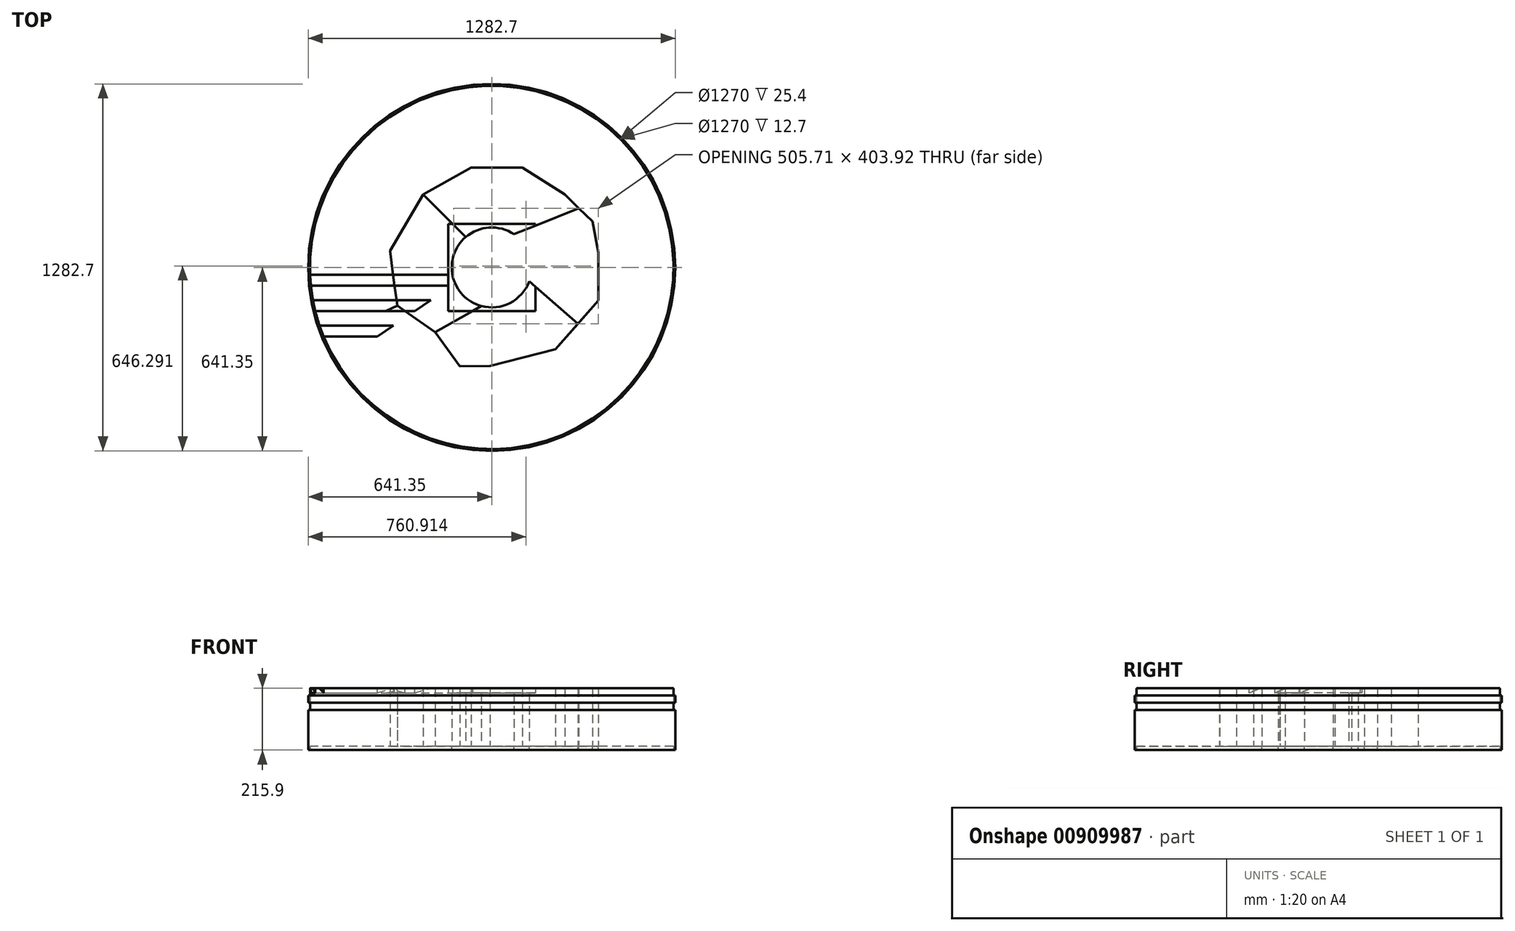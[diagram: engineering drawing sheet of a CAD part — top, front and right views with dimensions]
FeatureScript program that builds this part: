
annotation { "Feature Type Name" : "Feature", "Feature Type Description" : "" }
export const myFeature = defineFeature(function(context is Context, id is Id, definition is map)
    precondition{}
    {
        {
            var Q0;
            Q0=qCreatedBy(makeId("Top.planeOp"),FACE);
            var sketch = newSketch(context, id + "F0", { "sketchPlane" : qUnion([Q0])});
            skCircle(sketch, "E0", {"center": v(0, 0) * mm, "radius": 139.7 * mm});
            skCircle(sketch, "E1", {"center": v(0, 0) * mm, "radius": 635 * mm});
            skLineSegment(sketch, "E2", {"start": v(-36.54, -134.84) * mm, "end": v(-197.5, -226.73) * mm});
            skLineSegment(sketch, "E3", {"start": v(-197.5, -226.73) * mm, "end": v(-330.22, -133.5) * mm});
            skLineSegment(sketch, "E4", {"start": v(-330.22, -133.5) * mm, "end": v(-355.5, 57.67) * mm});
            skLineSegment(sketch, "E5", {"start": v(-355.5, 57.67) * mm, "end": v(-238.95, 255.32) * mm});
            skLineSegment(sketch, "E6", {"start": v(-238.95, 255.32) * mm, "end": v(-91, 106) * mm});
            skLineSegment(sketch, "E7", {"start": v(-238.95, 255.32) * mm, "end": v(-71.47, 348.54) * mm});
            skLineSegment(sketch, "E8", {"start": v(-71.47, 348.54) * mm, "end": v(107.07, 348.54) * mm});
            skLineSegment(sketch, "E9", {"start": v(107.07, 348.54) * mm, "end": v(255.58, 255.32) * mm});
            skLineSegment(sketch, "E10", {"start": v(255.58, 255.32) * mm, "end": v(303.56, 206.9) * mm});
            skLineSegment(sketch, "E11", {"start": v(303.56, 206.9) * mm, "end": v(77.5, 116.24) * mm});
            skLineSegment(sketch, "E12", {"start": v(77.5, 116.24) * mm, "end": v(303.56, 206.9) * mm});
            skLineSegment(sketch, "E13", {"start": v(303.56, 206.9) * mm, "end": v(351.96, 160.52) * mm});
            skLineSegment(sketch, "E14", {"start": v(351.96, 160.52) * mm, "end": v(372.42, 52.06) * mm});
            skLineSegment(sketch, "E15", {"start": v(372.42, 52.06) * mm, "end": v(372.42, -115.42) * mm});
            skLineSegment(sketch, "E16", {"start": v(372.42, -115.42) * mm, "end": v(301.18, -197.02) * mm});
            skLineSegment(sketch, "E17", {"start": v(301.18, -197.02) * mm, "end": v(223.18, -286.36) * mm});
            skLineSegment(sketch, "E18", {"start": v(223.18, -286.36) * mm, "end": v(-5.86, -344.53) * mm});
            skLineSegment(sketch, "E19", {"start": v(-5.86, -344.53) * mm, "end": v(-110.6, -345.22) * mm});
            skLineSegment(sketch, "E20", {"start": v(-110.6, -345.22) * mm, "end": v(-197.5, -226.73) * mm});
            skLineSegment(sketch, "E21", {"start": v(301.18, -197.02) * mm, "end": v(131.02, -48.47) * mm});
            skLineSegment(sketch, "E22", {"start": v(-330.22, -133.5) * mm, "end": v(-582.73, -252.28) * mm});
            skLineSegment(sketch, "E23", {"start": v(-355.5, 57.67) * mm, "end": v(-618.8, 142.52) * mm});
            skLineSegment(sketch, "E24", {"start": v(-238.95, 255.32) * mm, "end": v(-456.44, 441.46) * mm});
            skLineSegment(sketch, "E25", {"start": v(-71.47, 348.54) * mm, "end": v(-141.76, 618.97) * mm});
            skLineSegment(sketch, "E26", {"start": v(107.07, 348.54) * mm, "end": v(221.56, 595.1) * mm});
            skLineSegment(sketch, "E27", {"start": v(255.58, 255.32) * mm, "end": v(450.04, 447.98) * mm});
            skLineSegment(sketch, "E28", {"start": v(351.96, 160.52) * mm, "end": v(600.2, 207.35) * mm});
            skLineSegment(sketch, "E29", {"start": v(372.42, 52.06) * mm, "end": v(633.2, -47.9) * mm});
            skLineSegment(sketch, "E30", {"start": v(372.42, -115.42) * mm, "end": v(570.5, -278.85) * mm});
            skLineSegment(sketch, "E31", {"start": v(223.18, -286.36) * mm, "end": v(344.95, -533.14) * mm});
            skLineSegment(sketch, "E32", {"start": v(-5.86, -344.53) * mm, "end": v(67, -631.45) * mm});
            skLineSegment(sketch, "E33", {"start": v(-110.6, -345.22) * mm, "end": v(-330.26, -542.36) * mm});
            skCircle(sketch, "E34", {"center": v(0, 0) * mm, "radius": 641.35 * mm});
            skSolve(sketch);
        }
        {
            var Q0;
            Q0=makeQuery(id+"F0.imprint","IMPRINT",FACE,{"disambiguationData":[TD([[makeQuery(id+"F0.imprint","IMPRINT",EDGE,{"derivedFrom":sQuery(id+"F0.wireOp",EDGE,"E0")}),-1.0]])]});
            var Q1;
            {var subQ0=sQuery(id+"F0.wireOp",EDGE,"E12");Q1=makeQuery(id+"F0.imprint","IMPRINT",FACE,{"disambiguationData":[TD([[makeQuery(id+"F0.imprint","IMPRINT",EDGE,{"derivedFrom":subQ0}),-1.0]])]});}
            var Q2;
            Q2=makeQuery(id+"F0.imprint","IMPRINT",FACE,{"disambiguationData":[TD([[makeQuery(id+"F0.imprint","IMPRINT",EDGE,{"derivedFrom":sQuery(id+"F0.wireOp",EDGE,"E9")}),1.0]])]});
            var Q3;
            Q3=makeQuery(id+"F0.imprint","IMPRINT",FACE,{"disambiguationData":[TD([[makeQuery(id+"F0.imprint","IMPRINT",EDGE,{"derivedFrom":sQuery(id+"F0.wireOp",EDGE,"E7")}),1.0]])]});
            var Q4;
            Q4=makeQuery(id+"F0.imprint","IMPRINT",FACE,{"disambiguationData":[TD([[makeQuery(id+"F0.imprint","IMPRINT",EDGE,{"derivedFrom":sQuery(id+"F0.wireOp",EDGE,"E19")}),1.0]])]});
            extrude(context, id + "F1", {"entities" : qUnion([Q0, Q1, Q2, Q3, Q4]), "depth" : 203.2 * mm, "offsetDistance" : 25 * mm});
        }
        {
            var Q0;
            {var subQ0=sQuery(id+"F0.wireOp",EDGE,"E2");Q0=makeQuery(id+"F0.imprint","IMPRINT",FACE,{"disambiguationData":[TD([[makeQuery(id+"F0.imprint","IMPRINT",EDGE,{"derivedFrom":subQ0}),1.0]])]});}
            var Q1;
            {var subQ0=sQuery(id+"F0.wireOp",EDGE,"E6");Q1=makeQuery(id+"F0.imprint","IMPRINT",FACE,{"disambiguationData":[TD([[makeQuery(id+"F0.imprint","IMPRINT",EDGE,{"derivedFrom":subQ0}),1.0]])]});}
            var Q2;
            Q2=makeQuery(id+"F0.imprint","IMPRINT",FACE,{"disambiguationData":[TD([[makeQuery(id+"F0.imprint","IMPRINT",EDGE,{"derivedFrom":sQuery(id+"F0.wireOp",EDGE,"E15")}),1.0]])]});
            var Q3;
            Q3=makeQuery(id+"F0.imprint","IMPRINT",FACE,{"disambiguationData":[TD([[makeQuery(id+"F0.imprint","IMPRINT",EDGE,{"derivedFrom":sQuery(id+"F0.wireOp",EDGE,"E4")}),1.0]])]});
            extrude(context, id + "F2", {"entities" : qUnion([Q0, Q1, Q2, Q3]), "depth" : 203.2 * mm, "offsetDistance" : 25 * mm});
        }
        {
            var Q0;
            Q0=makeQuery(id+"F0.imprint","IMPRINT",FACE,{"disambiguationData":[TD([[makeQuery(id+"F0.imprint","IMPRINT",EDGE,{"derivedFrom":sQuery(id+"F0.wireOp",EDGE,"E18")}),1.0]])]});
            var Q1;
            Q1=makeQuery(id+"F0.imprint","IMPRINT",FACE,{"disambiguationData":[TD([[makeQuery(id+"F0.imprint","IMPRINT",EDGE,{"derivedFrom":sQuery(id+"F0.wireOp",EDGE,"E3")}),1.0]])]});
            var Q2;
            Q2=makeQuery(id+"F0.imprint","IMPRINT",FACE,{"disambiguationData":[TD([[makeQuery(id+"F0.imprint","IMPRINT",EDGE,{"derivedFrom":sQuery(id+"F0.wireOp",EDGE,"E5")}),1.0]])]});
            var Q3;
            Q3=makeQuery(id+"F0.imprint","IMPRINT",FACE,{"disambiguationData":[TD([[makeQuery(id+"F0.imprint","IMPRINT",EDGE,{"derivedFrom":sQuery(id+"F0.wireOp",EDGE,"E8")}),1.0]])]});
            var Q4;
            Q4=makeQuery(id+"F0.imprint","IMPRINT",FACE,{"disambiguationData":[TD([[makeQuery(id+"F0.imprint","IMPRINT",EDGE,{"derivedFrom":sQuery(id+"F0.wireOp",EDGE,"E10")}),1.0]])]});
            extrude(context, id + "F3", {"entities" : qUnion([Q0, Q1, Q2, Q3, Q4]), "depth" : 203.2 * mm, "offsetDistance" : 25 * mm});
        }
        {
            var Q0;
            Q0=makeQuery(id+"F0.imprint","IMPRINT",FACE,{"disambiguationData":[TD([[makeQuery(id+"F0.imprint","IMPRINT",EDGE,{"derivedFrom":sQuery(id+"F0.wireOp",EDGE,"E16")}),1.0]])]});
            var Q1;
            Q1=makeQuery(id+"F0.imprint","IMPRINT",FACE,{"disambiguationData":[TD([[makeQuery(id+"F0.imprint","IMPRINT",EDGE,{"derivedFrom":sQuery(id+"F0.wireOp",EDGE,"E14")}),1.0]])]});
            extrude(context, id + "F4", {"entities" : qUnion([Q0, Q1]), "depth" : 203.2 * mm, "offsetDistance" : 25 * mm});
        }
        {
            var Q0;
            Q0=makeQuery(id+"F1.opExtrude","CAP_FACE",FACE,{"disambiguationData":[OSD([sQuery(id+"F0.wireOp",EDGE,"E0"),sQuery(id+"F0.wireOp",EDGE,"E1")])],"isStart":false});
            var sketch = newSketch(context, id + "F5", { "sketchPlane" : qUnion([Q0])});
            skLineSegment(sketch, "E35.bottom", {"start": v(-634.5, -25.4) * mm, "end": v(-138.54, -25.4) * mm});
            skLineSegment(sketch, "E35.top", {"start": v(-634.5, -63.5) * mm, "end": v(-138.54, -63.5) * mm});
            skLineSegment(sketch, "E35.left", {"start": v(-634.5, -25.4) * mm, "end": v(-634.5, -63.5) * mm});
            skLineSegment(sketch, "E35.right", {"start": v(-138.54, -25.4) * mm, "end": v(-138.54, -63.5) * mm});
            skLineSegment(sketch, "E36.bottom", {"start": v(-624.63, -114.3) * mm, "end": v(-213.24, -114.3) * mm});
            skLineSegment(sketch, "E36.top", {"start": v(-624.63, -152.4) * mm, "end": v(-269.26, -152.4) * mm});
            skLineSegment(sketch, "E36.left", {"start": v(-624.63, -114.3) * mm, "end": v(-624.63, -152.4) * mm});
            skLineSegment(sketch, "E37.bottom", {"start": v(-601.61, -203.2) * mm, "end": v(-343.96, -203.2) * mm});
            skLineSegment(sketch, "E37.top", {"start": v(-601.61, -241.3) * mm, "end": v(-399.98, -241.3) * mm});
            skLineSegment(sketch, "E37.left", {"start": v(-601.61, -203.2) * mm, "end": v(-601.61, -241.3) * mm});
            skLineSegment(sketch, "E38", {"start": v(-444.25, -25.4) * mm, "end": v(-444.25, -114.3) * mm, "construction": true});
            skLineSegment(sketch, "E39", {"start": v(-444.25, -114.3) * mm, "end": v(-444.25, -203.2) * mm, "construction": true});
            skLineSegment(sketch, "E40", {"start": v(-213.24, -114.3) * mm, "end": v(-269.26, -152.4) * mm});
            skLineSegment(sketch, "E41", {"start": v(-343.96, -203.2) * mm, "end": v(-399.98, -241.3) * mm});
            skCircle(sketch, "E42", {"center": v(0, 0) * mm, "radius": 152.4 * mm});
            skLineSegment(sketch, "E43.bottom", {"start": v(-152.4, 152.4) * mm, "end": v(152.4, 152.4) * mm});
            skLineSegment(sketch, "E43.top", {"start": v(-152.4, -152.4) * mm, "end": v(152.4, -152.4) * mm});
            skLineSegment(sketch, "E43.left", {"start": v(-152.4, 152.4) * mm, "end": v(-152.4, -152.4) * mm});
            skLineSegment(sketch, "E43.right", {"start": v(152.4, 152.4) * mm, "end": v(152.4, -152.4) * mm});
            skLineSegment(sketch, "E44", {"start": v(0, 152.4) * mm, "end": v(0, -152.4) * mm, "construction": true});
            skLineSegment(sketch, "E45", {"start": v(152.4, 0) * mm, "end": v(-152.4, 0) * mm, "construction": true});
            skSolve(sketch);
        }
        {
            var Q0;
            {var subQ0=sQuery(id+"F5.wireOp",EDGE,"E36.bottom");Q0=makeQuery(id+"F5.imprint","IMPRINT",FACE,{"disambiguationData":[TD([[makeQuery(id+"F5.imprint","IMPRINT",EDGE,{"derivedFrom":subQ0}),-1.0]])]});}
            var Q1;
            {var subQ0=sQuery(id+"F5.wireOp",EDGE,"E37.bottom");Q1=makeQuery(id+"F5.imprint","IMPRINT",FACE,{"disambiguationData":[TD([[makeQuery(id+"F5.imprint","IMPRINT",EDGE,{"derivedFrom":subQ0}),-1.0]])]});}
            var Q2;
            {var subQ0=sQuery(id+"F5.wireOp",EDGE,"E35.left");Q2=makeQuery(id+"F5.imprint","IMPRINT",FACE,{"disambiguationData":[TD([[makeQuery(id+"F5.imprint","IMPRINT",EDGE,{"derivedFrom":subQ0}),1.0]])]});}
            var Q3;
            {var subQ0=sQuery(id+"F5.wireOp",EDGE,"E43.left");var subQ1=sQuery(id+"F5.wireOp",EDGE,"E35.bottom");var subQ2=makeQuery(id+"F5.imprint","INTERSECT",VERTEX,{"derivedFrom":[subQ1,subQ0]});Q3=makeQuery(id+"F5.imprint","IMPRINT",FACE,{"disambiguationData":[TD([[makeQuery(id+"F5.imprint","IMPRINT",EDGE,{"disambiguationData":[TD([[subQ2,-1.0]])],"derivedFrom":subQ1}),-1.0]])]});}
            extrude(context, id + "F6", {"entities" : qUnion([Q0, Q1, Q2, Q3]), "operationType" : NewBodyOperationType.REMOVE, "oppositeDirection" : true, "depth" : 15.88 * mm, "offsetDistance" : 25 * mm});
        }
        {
            var Q0;
            Q0=makeQuery(id+"F6.boolean.opBoolean","COPY",EDGE,{"derivedFrom":makeQuery(id+"F6.opExtrude","CAP_EDGE",EDGE,{"disambiguationData":[OSD([sQuery(id+"F5.wireOp",EDGE,"E35.bottom")])],"isStart":false})});
            var Q1;
            Q1=makeQuery(id+"F6.boolean.opBoolean","COPY",EDGE,{"derivedFrom":makeQuery(id+"F6.opExtrude","CAP_EDGE",EDGE,{"disambiguationData":[OSD([sQuery(id+"F5.wireOp",EDGE,"E36.bottom")])],"isStart":false})});
            var Q2;
            Q2=makeQuery(id+"F6.boolean.opBoolean","COPY",EDGE,{"derivedFrom":makeQuery(id+"F6.opExtrude","CAP_EDGE",EDGE,{"disambiguationData":[OSD([sQuery(id+"F5.wireOp",EDGE,"E37.bottom")])],"isStart":false})});
            chamfer(context, id + "F7", {"entities" : qUnion([Q0, Q1, Q2]), "chamferType" : ChamferType.TWO_OFFSETS, "width1" : 15.88 * mm, "oppositeDirection" : false, "width2" : 38.1 * mm, "tangentPropagation" : true});
        }
        {
            var Q0;
            {var subQ0=sQuery(id+"F5.wireOp",EDGE,"E42");var subQ1=sQuery(id+"F5.wireOp",EDGE,"E35.bottom");var subQ2=makeQuery(id+"F5.imprint","INTERSECT",VERTEX,{"derivedFrom":[subQ1,subQ0]});Q0=makeQuery(id+"F5.imprint","IMPRINT",FACE,{"disambiguationData":[TD([[makeQuery(id+"F5.imprint","IMPRINT",EDGE,{"disambiguationData":[TD([[subQ2,-1.0]])],"derivedFrom":subQ1}),-1.0]])]});}
            var Q1;
            {var subQ0=sQuery(id+"F5.wireOp",EDGE,"E42");var subQ1=sQuery(id+"F5.wireOp",EDGE,"E35.bottom");var subQ2=makeQuery(id+"F5.imprint","INTERSECT",VERTEX,{"derivedFrom":[subQ1,subQ0]});Q1=makeQuery(id+"F5.imprint","IMPRINT",FACE,{"disambiguationData":[TD([[makeQuery(id+"F5.imprint","IMPRINT",EDGE,{"disambiguationData":[TD([[subQ2,-1.0]])],"derivedFrom":subQ1}),1.0]])]});}
            var Q2;
            {var subQ0=sQuery(id+"F5.wireOp",EDGE,"E43.bottom");var subQ1=sQuery(id+"F5.wireOp",EDGE,"E42");var subQ2=makeQuery(id+"F5.imprint","INTERSECT",VERTEX,{"derivedFrom":[subQ1,subQ0]});Q2=makeQuery(id+"F5.imprint","IMPRINT",FACE,{"disambiguationData":[TD([[makeQuery(id+"F5.imprint","IMPRINT",EDGE,{"disambiguationData":[TD([[subQ2,-1.0]])],"derivedFrom":subQ1}),-1.0]])]});}
            var Q3;
            {var subQ0=sQuery(id+"F5.wireOp",EDGE,"E43.bottom");var subQ1=sQuery(id+"F5.wireOp",EDGE,"E42");var subQ2=makeQuery(id+"F5.imprint","INTERSECT",VERTEX,{"derivedFrom":[subQ1,subQ0]});Q3=makeQuery(id+"F5.imprint","IMPRINT",FACE,{"disambiguationData":[TD([[makeQuery(id+"F5.imprint","IMPRINT",EDGE,{"disambiguationData":[TD([[subQ2,1.0]])],"derivedFrom":subQ1}),-1.0]])]});}
            var Q4;
            {var subQ0=sQuery(id+"F5.wireOp",EDGE,"E43.right");var subQ1=sQuery(id+"F5.wireOp",EDGE,"E42");var subQ2=makeQuery(id+"F5.imprint","INTERSECT",VERTEX,{"derivedFrom":[subQ1,subQ0]});Q4=makeQuery(id+"F5.imprint","IMPRINT",FACE,{"disambiguationData":[TD([[makeQuery(id+"F5.imprint","IMPRINT",EDGE,{"disambiguationData":[TD([[subQ2,1.0]])],"derivedFrom":subQ1}),-1.0]])]});}
            var Q5;
            {var subQ3=sQuery(id+"F5.wireOp",EDGE,"E43.left");var subQ5=sQuery(id+"F5.wireOp",EDGE,"E43.top");var subQ7=makeQuery(id+"F5.imprint","INTERSECT",VERTEX,{"derivedFrom":[subQ5,subQ3]});Q5=makeQuery(id+"F5.imprint","IMPRINT",FACE,{"disambiguationData":[TD([[makeQuery(id+"F5.imprint","IMPRINT",EDGE,{"disambiguationData":[TD([[subQ7,-1.0]])],"derivedFrom":subQ5}),1.0]])]});}
            var Q6;
            {var subQ0=sQuery(id+"F5.wireOp",EDGE,"E43.left");var subQ1=sQuery(id+"F5.wireOp",EDGE,"E35.bottom");var subQ2=makeQuery(id+"F5.imprint","INTERSECT",VERTEX,{"derivedFrom":[subQ1,subQ0]});Q6=makeQuery(id+"F5.imprint","IMPRINT",FACE,{"disambiguationData":[TD([[makeQuery(id+"F5.imprint","IMPRINT",EDGE,{"disambiguationData":[TD([[subQ2,-1.0]])],"derivedFrom":subQ1}),-1.0]])]});}
            var Q7;
            {var subQ0=sQuery(id+"F5.wireOp",EDGE,"E43.left");var subQ1=sQuery(id+"F5.wireOp",EDGE,"E35.bottom");var subQ2=makeQuery(id+"F5.imprint","INTERSECT",VERTEX,{"derivedFrom":[subQ1,subQ0]});Q7=makeQuery(id+"F5.imprint","IMPRINT",FACE,{"disambiguationData":[TD([[makeQuery(id+"F5.imprint","IMPRINT",EDGE,{"disambiguationData":[TD([[subQ2,-1.0]])],"derivedFrom":subQ1}),1.0]])]});}
            var Q8;
            Q8=makeQuery(id+"F6.boolean.opBoolean","COPY",FACE,{"derivedFrom":makeQuery(id+"F6.opExtrude","CAP_FACE",FACE,{"disambiguationData":[OSD([sQuery(id+"F0.wireOp",EDGE,"E1"),sQuery(id+"F5.wireOp",EDGE,"E35.bottom"),sQuery(id+"F5.wireOp",EDGE,"E35.top"),sQuery(id+"F5.wireOp",EDGE,"E42")])],"isStart":false})});
            extrude(context, id + "F8", {"entities" : qUnion([Q0, Q1, Q2, Q3, Q4, Q5, Q6, Q7]), "operationType" : NewBodyOperationType.REMOVE, "oppositeDirection" : true, "depth" : 15.88 * mm, "endBoundEntityFace" : qUnion([Q8]), "offsetDistance" : 25 * mm});
        }
        {
            var Q0;
            Q0=makeQuery(id+"F0.imprint","IMPRINT",FACE,{"disambiguationData":[TD([[makeQuery(id+"F0.imprint","IMPRINT",EDGE,{"derivedFrom":sQuery(id+"F0.wireOp",EDGE,"E34")}),1.0]])]});
            extrude(context, id + "F9", {"entities" : qUnion([Q0]), "depth" : 177.8 * mm, "offsetDistance" : 25 * mm});
        }
        {
            var Q0;
            Q0=makeQuery(id+"F0.imprint","IMPRINT",FACE,{"disambiguationData":[TD([[makeQuery(id+"F0.imprint","IMPRINT",EDGE,{"derivedFrom":sQuery(id+"F0.wireOp",EDGE,"E34")}),1.0]])]});
            extrude(context, id + "F10", {"entities" : qUnion([Q0]), "operationType" : NewBodyOperationType.REMOVE, "depth" : 152.4 * mm, "offsetDistance" : 25 * mm});
        }
        {
            var Q0;
            Q0=makeQuery(id+"F0.imprint","IMPRINT",FACE,{"disambiguationData":[TD([[makeQuery(id+"F0.imprint","IMPRINT",EDGE,{"derivedFrom":sQuery(id+"F0.wireOp",EDGE,"E34")}),1.0]])]});
            extrude(context, id + "F11", {"entities" : qUnion([Q0]), "depth" : 127 * mm, "offsetDistance" : 25 * mm});
        }
        {
            var Q0;
            Q0=makeQuery(id+"F0.imprint","IMPRINT",FACE,{"disambiguationData":[TD([[makeQuery(id+"F0.imprint","IMPRINT",EDGE,{"derivedFrom":sQuery(id+"F0.wireOp",EDGE,"E34")}),1.0]])]});
            extrude(context, id + "F12", {"entities" : qUnion([Q0]), "operationType" : NewBodyOperationType.ADD, "oppositeDirection" : true, "depth" : 12.7 * mm, "offsetDistance" : 25 * mm});
        }
        {
            var Q0;
            Q0=makeQuery(id+"F0.imprint","IMPRINT",FACE,{"disambiguationData":[TD([[makeQuery(id+"F0.imprint","IMPRINT",EDGE,{"derivedFrom":sQuery(id+"F0.wireOp",EDGE,"E18")}),1.0]])]});
            var Q1;
            Q1=makeQuery(id+"F0.imprint","IMPRINT",FACE,{"disambiguationData":[TD([[makeQuery(id+"F0.imprint","IMPRINT",EDGE,{"derivedFrom":sQuery(id+"F0.wireOp",EDGE,"E16")}),1.0]])]});
            var Q2;
            Q2=makeQuery(id+"F0.imprint","IMPRINT",FACE,{"disambiguationData":[TD([[makeQuery(id+"F0.imprint","IMPRINT",EDGE,{"derivedFrom":sQuery(id+"F0.wireOp",EDGE,"E15")}),1.0]])]});
            var Q3;
            Q3=makeQuery(id+"F0.imprint","IMPRINT",FACE,{"disambiguationData":[TD([[makeQuery(id+"F0.imprint","IMPRINT",EDGE,{"derivedFrom":sQuery(id+"F0.wireOp",EDGE,"E14")}),1.0]])]});
            var Q4;
            Q4=makeQuery(id+"F0.imprint","IMPRINT",FACE,{"disambiguationData":[TD([[makeQuery(id+"F0.imprint","IMPRINT",EDGE,{"derivedFrom":sQuery(id+"F0.wireOp",EDGE,"E10")}),1.0]])]});
            var Q5;
            Q5=makeQuery(id+"F0.imprint","IMPRINT",FACE,{"disambiguationData":[TD([[makeQuery(id+"F0.imprint","IMPRINT",EDGE,{"derivedFrom":sQuery(id+"F0.wireOp",EDGE,"E9")}),1.0]])]});
            var Q6;
            Q6=makeQuery(id+"F0.imprint","IMPRINT",FACE,{"disambiguationData":[TD([[makeQuery(id+"F0.imprint","IMPRINT",EDGE,{"derivedFrom":sQuery(id+"F0.wireOp",EDGE,"E8")}),1.0]])]});
            var Q7;
            Q7=makeQuery(id+"F0.imprint","IMPRINT",FACE,{"disambiguationData":[TD([[makeQuery(id+"F0.imprint","IMPRINT",EDGE,{"derivedFrom":sQuery(id+"F0.wireOp",EDGE,"E7")}),1.0]])]});
            var Q8;
            Q8=makeQuery(id+"F0.imprint","IMPRINT",FACE,{"disambiguationData":[TD([[makeQuery(id+"F0.imprint","IMPRINT",EDGE,{"derivedFrom":sQuery(id+"F0.wireOp",EDGE,"E5")}),1.0]])]});
            var Q9;
            Q9=makeQuery(id+"F0.imprint","IMPRINT",FACE,{"disambiguationData":[TD([[makeQuery(id+"F0.imprint","IMPRINT",EDGE,{"derivedFrom":sQuery(id+"F0.wireOp",EDGE,"E4")}),1.0]])]});
            var Q10;
            Q10=makeQuery(id+"F0.imprint","IMPRINT",FACE,{"disambiguationData":[TD([[makeQuery(id+"F0.imprint","IMPRINT",EDGE,{"derivedFrom":sQuery(id+"F0.wireOp",EDGE,"E3")}),1.0]])]});
            var Q11;
            Q11=makeQuery(id+"F0.imprint","IMPRINT",FACE,{"disambiguationData":[TD([[makeQuery(id+"F0.imprint","IMPRINT",EDGE,{"derivedFrom":sQuery(id+"F0.wireOp",EDGE,"E19")}),1.0]])]});
            var Q12;
            {var subQ0=sQuery(id+"F0.wireOp",EDGE,"E2");Q12=makeQuery(id+"F0.imprint","IMPRINT",FACE,{"disambiguationData":[TD([[makeQuery(id+"F0.imprint","IMPRINT",EDGE,{"derivedFrom":subQ0}),1.0]])]});}
            var Q13;
            {var subQ0=sQuery(id+"F0.wireOp",EDGE,"E12");Q13=makeQuery(id+"F0.imprint","IMPRINT",FACE,{"disambiguationData":[TD([[makeQuery(id+"F0.imprint","IMPRINT",EDGE,{"derivedFrom":subQ0}),-1.0]])]});}
            var Q14;
            {var subQ0=sQuery(id+"F0.wireOp",EDGE,"E6");Q14=makeQuery(id+"F0.imprint","IMPRINT",FACE,{"disambiguationData":[TD([[makeQuery(id+"F0.imprint","IMPRINT",EDGE,{"derivedFrom":subQ0}),1.0]])]});}
            var Q15;
            {var subQ0=sQuery(id+"F0.wireOp",EDGE,"E2");Q15=makeQuery(id+"F0.imprint","IMPRINT",FACE,{"disambiguationData":[TD([[makeQuery(id+"F0.imprint","IMPRINT",EDGE,{"derivedFrom":subQ0}),-1.0]])]});}
            extrude(context, id + "F13", {"entities" : qUnion([Q0, Q1, Q2, Q3, Q4, Q5, Q6, Q7, Q8, Q9, Q10, Q11, Q12, Q13, Q14, Q15]), "oppositeDirection" : true, "depth" : 12.7 * mm, "offsetDistance" : 25 * mm});
        }
    });
